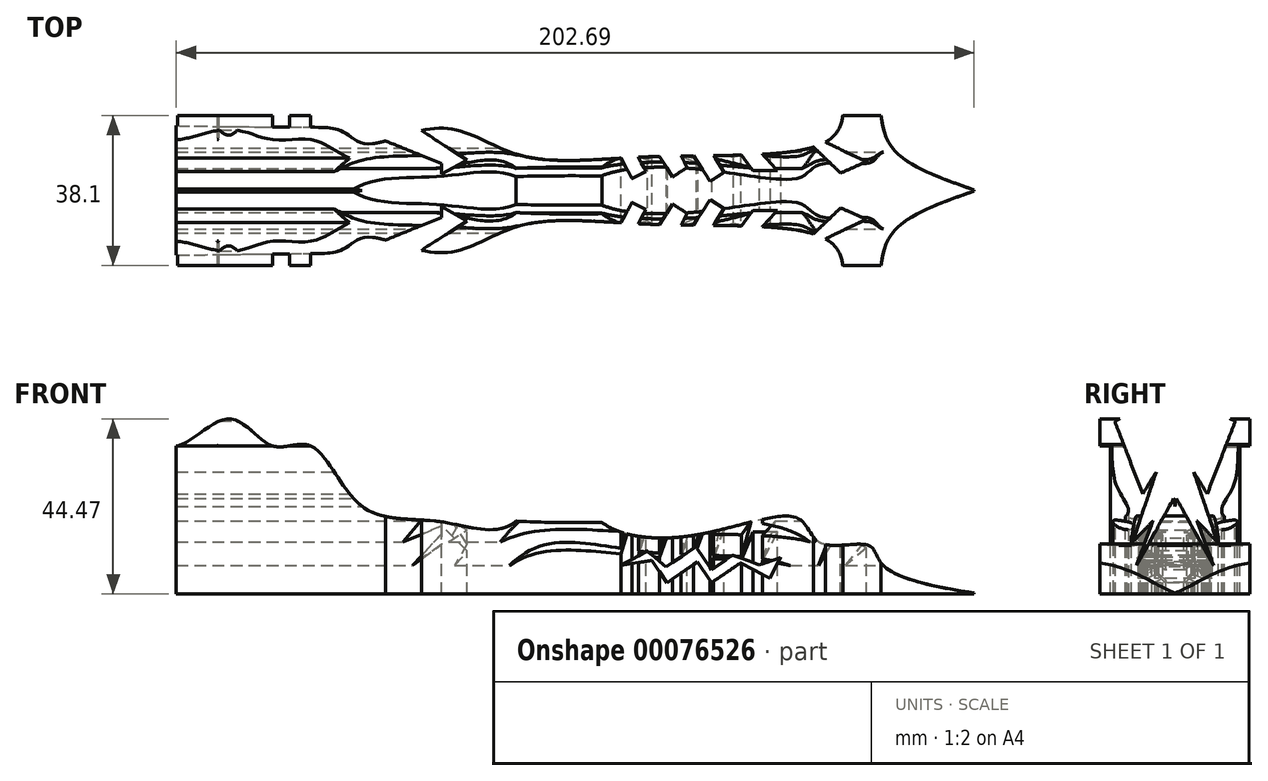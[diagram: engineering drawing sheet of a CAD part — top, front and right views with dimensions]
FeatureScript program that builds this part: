
annotation { "Feature Type Name" : "Feature", "Feature Type Description" : "" }
export const myFeature = defineFeature(function(context is Context, id is Id, definition is map)
    precondition{}
    {
        {
            var Q0;
            Q0=qCreatedBy(makeId("Front.planeOp"),FACE);
            var sketch = newSketch(context, id + "F0", { "sketchPlane" : qUnion([Q0])});
            skLineSegment(sketch, "E0", {"start": v(-67.36, 23) * mm, "end": v(-67.36, -37.65) * mm});
            skLineSegment(sketch, "E1", {"start": v(-67.36, -37.65) * mm, "end": v(135.33, -37.65) * mm});
            skLineSegment(sketch, "E2", {"start": v(135.33, -37.65) * mm, "end": v(135.33, -19.94) * mm});
            skLineSegment(sketch, "E3", {"start": v(135.33, -19.94) * mm, "end": v(-67.36, 23) * mm});
            skSolve(sketch);
        }
        {
            var Q0;
            Q0=makeQuery(id+"F0.imprint","IMPRINT",FACE,{"disambiguationData":[TD([[makeQuery(id+"F0.imprint","IMPRINT",EDGE,{"derivedFrom":sQuery(id+"F0.wireOp",EDGE,"E0")}),1.0]])]});
            extrude(context, id + "F1", {"entities" : qUnion([Q0]), "endBound" : BoundingType.SYMMETRIC, "depth" : 38.1 * mm});
        }
        {
            var Q0;
            Q0=qCreatedBy(makeId("Front.planeOp"),FACE);
            var sketch = newSketch(context, id + "F2", { "sketchPlane" : qUnion([Q0])});
            skFitSpline(sketch, "E4", {"points": [v(-67.52, 10.01) * mm, v(-37.25, 9.08) * mm, v(-13.04, -13.04) * mm, v(96.84, -16.76) * mm, v(119.66, -21.65) * mm, v(136.89, -38.41) * mm, v(148.53, -53.78) * mm, v(0, -97.08) * mm, v(-109.89, -27.47) * mm, v(-68.68, -141.31) * mm, v(197.42, -89.86) * mm, v(91.72, 90.8) * mm, v(-73.1, 52.85) * mm, v(-99.88, 21.65) * mm, v(-67.52, 10.01) * mm]});
            skSolve(sketch);
        }
        {
            var Q0;
            Q0=makeQuery(id+"F2.imprint","IMPRINT",FACE,{"disambiguationData":[TD([[makeQuery(id+"F2.imprint","IMPRINT",EDGE,{"derivedFrom":sQuery(id+"F2.wireOp",EDGE,"E4")}),1.0]])]});
            extrude(context, id + "F3", {"entities" : qUnion([Q0]), "operationType" : NewBodyOperationType.REMOVE, "endBound" : BoundingType.SYMMETRIC, "oppositeDirection" : true, "depth" : 38.1 * mm});
        }
        {
            var Q0;
            Q0=qCreatedBy(makeId("Top.planeOp"),FACE);
            var sketch = newSketch(context, id + "F4", { "sketchPlane" : qUnion([Q0])});
            skFitSpline(sketch, "E5", {"points": [v(-73.1, 16.53) * mm, v(-34.7, 16.06) * mm, v(-24.91, 14.9) * mm, v(-19.1, 11.87) * mm, v(0, 15.83) * mm, v(19.55, 9.08) * mm, v(54, 8.61) * mm, v(95.68, 11.4) * mm, v(101.97, 19.1) * mm, v(102.9, 29.1) * mm, v(109.42, 27.94) * mm, v(111.74, 18.86) * mm, v(115.7, 9.55) * mm, v(135.72, 0) * mm], "startDerivative": vector(378.98, -5.81) * mm, "endDerivative": vector(270.52, -94.72) * mm});
            skFitSpline(sketch, "E6.MirrorCS", {"points": [v(-73.1, -16.53) * mm, v(-34.7, -16.06) * mm, v(-24.91, -14.9) * mm, v(-19.1, -11.87) * mm, v(0, -15.83) * mm, v(19.55, -9.08) * mm, v(54, -8.61) * mm, v(95.68, -11.4) * mm, v(101.97, -19.1) * mm, v(102.9, -29.1) * mm, v(109.42, -27.94) * mm, v(111.74, -18.86) * mm, v(115.7, -9.55) * mm, v(135.72, 0) * mm], "startDerivative": vector(378.98, 5.81) * mm, "endDerivative": vector(270.52, 94.72) * mm});
            skLineSegment(sketch, "E7", {"start": v(-73.1, -16.53) * mm, "end": v(-73.1, -54.3) * mm});
            skLineSegment(sketch, "E8", {"start": v(-73.1, -54.3) * mm, "end": v(204.06, -34.02) * mm});
            skLineSegment(sketch, "E9", {"start": v(204.06, -34.02) * mm, "end": v(136.25, 78.53) * mm});
            skLineSegment(sketch, "E10", {"start": v(136.25, 78.53) * mm, "end": v(-81.16, 49.17) * mm});
            skLineSegment(sketch, "E11", {"start": v(-81.16, 49.17) * mm, "end": v(-73.1, 16.53) * mm});
            skSolve(sketch);
        }
        {
            var Q0;
            Q0=makeQuery(id+"F4.imprint","IMPRINT",FACE,{"disambiguationData":[TD([[makeQuery(id+"F4.imprint","IMPRINT",EDGE,{"derivedFrom":sQuery(id+"F4.wireOp",EDGE,"E5")}),1.0]])]});
            extrude(context, id + "F5", {"entities" : qUnion([Q0]), "operationType" : NewBodyOperationType.REMOVE, "endBound" : BoundingType.THROUGH_ALL, "oppositeDirection" : true, "depth" : 25.4 * mm});
        }
        {
            var Q0;
            Q0=qCreatedBy(makeId("Top.planeOp"),FACE);
            var sketch = newSketch(context, id + "F6", { "sketchPlane" : qUnion([Q0])});
            skLineSegment(sketch, "E12", {"start": v(94.91, 13.54) * mm, "end": v(107.95, 7.32) * mm});
            skLineSegment(sketch, "E13", {"start": v(107.95, 7.32) * mm, "end": v(101.43, 4.42) * mm});
            skPoint(sketch, "E13.endSnap0", {"position": v(101.43, 10.43) * mm});
            skLineSegment(sketch, "E14", {"start": v(101.43, 4.42) * mm, "end": v(86.62, 18.64) * mm});
            skLineSegment(sketch, "E15", {"start": v(86.62, 18.64) * mm, "end": v(94.91, 13.54) * mm});
            skLineSegment(sketch, "E16.MirrorCS", {"start": v(101.43, -4.42) * mm, "end": v(86.62, -18.64) * mm});
            skLineSegment(sketch, "E17.MirrorCS", {"start": v(107.95, -7.32) * mm, "end": v(101.43, -4.42) * mm});
            skLineSegment(sketch, "E18.MirrorCS", {"start": v(94.91, -13.54) * mm, "end": v(107.95, -7.32) * mm});
            skLineSegment(sketch, "E19.MirrorCS", {"start": v(86.62, -18.64) * mm, "end": v(94.91, -13.54) * mm});
            skSolve(sketch);
        }
        {
            var Q0;
            Q0=qCreatedBy(makeId("Top.planeOp"),FACE);
            var sketch = newSketch(context, id + "F7", { "sketchPlane" : qUnion([Q0])});
            skLineSegment(sketch, "E20", {"start": v(78.2, 12.72) * mm, "end": v(85.44, 5.08) * mm});
            skLineSegment(sketch, "E21", {"start": v(85.44, 5.08) * mm, "end": v(79.12, 5.08) * mm});
            skLineSegment(sketch, "E22", {"start": v(79.12, 5.08) * mm, "end": v(70.92, 16.06) * mm});
            skLineSegment(sketch, "E23", {"start": v(70.92, 16.06) * mm, "end": v(78.2, 12.72) * mm});
            skLineSegment(sketch, "E24", {"start": v(65.06, 15.1) * mm, "end": v(71.84, 4.63) * mm});
            skLineSegment(sketch, "E25", {"start": v(71.84, 4.63) * mm, "end": v(68.27, 2.32) * mm});
            skLineSegment(sketch, "E26", {"start": v(68.27, 2.32) * mm, "end": v(60, 15.12) * mm});
            skLineSegment(sketch, "E27", {"start": v(60, 15.12) * mm, "end": v(65.06, 15.1) * mm});
            skLineSegment(sketch, "E28", {"start": v(62.45, 5.83) * mm, "end": v(58.77, 3.46) * mm});
            skLineSegment(sketch, "E29", {"start": v(58.77, 3.46) * mm, "end": v(51.13, 15.27) * mm});
            skLineSegment(sketch, "E30", {"start": v(51.13, 15.27) * mm, "end": v(57.58, 15.27) * mm});
            skLineSegment(sketch, "E31", {"start": v(57.58, 15.27) * mm, "end": v(62.45, 5.83) * mm});
            skLineSegment(sketch, "E32", {"start": v(48.56, 11.18) * mm, "end": v(51.93, 4.88) * mm});
            skLineSegment(sketch, "E33", {"start": v(51.93, 4.88) * mm, "end": v(48.44, 3.02) * mm});
            skLineSegment(sketch, "E34", {"start": v(48.44, 3.02) * mm, "end": v(42.75, 13.7) * mm});
            skLineSegment(sketch, "E35", {"start": v(42.75, 13.7) * mm, "end": v(48.56, 11.18) * mm});
            skLineSegment(sketch, "E36", {"start": v(-18.37, 14.29) * mm, "end": v(0, 6.83) * mm});
            skLineSegment(sketch, "E37", {"start": v(0, 6.83) * mm, "end": v(0, 4.12) * mm});
            skLineSegment(sketch, "E38", {"start": v(0, 4.12) * mm, "end": v(6.58, 7.77) * mm});
            skLineSegment(sketch, "E39", {"start": v(6.58, 7.77) * mm, "end": v(-18.03, 23.44) * mm});
            skLineSegment(sketch, "E40", {"start": v(-18.03, 23.44) * mm, "end": v(-18.37, 14.29) * mm});
            skLineSegment(sketch, "E41.MirrorCS", {"start": v(6.58, -7.77) * mm, "end": v(-18.03, -23.44) * mm});
            skLineSegment(sketch, "E42.MirrorCS", {"start": v(-18.37, -14.29) * mm, "end": v(0, -6.83) * mm});
            skLineSegment(sketch, "E43.MirrorCS", {"start": v(-18.03, -23.44) * mm, "end": v(-18.37, -14.29) * mm});
            skLineSegment(sketch, "E44.MirrorCS", {"start": v(0, -4.12) * mm, "end": v(6.58, -7.77) * mm});
            skLineSegment(sketch, "E45.MirrorCS", {"start": v(0, -6.83) * mm, "end": v(0, -4.12) * mm});
            skLineSegment(sketch, "E46.MirrorCS", {"start": v(48.44, -3.02) * mm, "end": v(42.75, -13.7) * mm});
            skLineSegment(sketch, "E47.MirrorCS", {"start": v(42.75, -13.7) * mm, "end": v(48.56, -11.18) * mm});
            skLineSegment(sketch, "E48.MirrorCS", {"start": v(48.56, -11.18) * mm, "end": v(51.93, -4.88) * mm});
            skLineSegment(sketch, "E49.MirrorCS", {"start": v(51.93, -4.88) * mm, "end": v(48.44, -3.02) * mm});
            skLineSegment(sketch, "E50.MirrorCS", {"start": v(62.45, -5.83) * mm, "end": v(58.77, -3.46) * mm});
            skLineSegment(sketch, "E51.MirrorCS", {"start": v(58.77, -3.46) * mm, "end": v(51.13, -15.27) * mm});
            skLineSegment(sketch, "E52.MirrorCS", {"start": v(57.58, -15.27) * mm, "end": v(62.45, -5.83) * mm});
            skLineSegment(sketch, "E53.MirrorCS", {"start": v(51.13, -15.27) * mm, "end": v(57.58, -15.27) * mm});
            skLineSegment(sketch, "E54.MirrorCS", {"start": v(60, -15.12) * mm, "end": v(65.06, -15.1) * mm});
            skLineSegment(sketch, "E55.MirrorCS", {"start": v(68.27, -2.32) * mm, "end": v(60, -15.12) * mm});
            skLineSegment(sketch, "E56.MirrorCS", {"start": v(71.84, -4.63) * mm, "end": v(68.27, -2.32) * mm});
            skLineSegment(sketch, "E57.MirrorCS", {"start": v(65.06, -15.1) * mm, "end": v(71.84, -4.63) * mm});
            skLineSegment(sketch, "E58.MirrorCS", {"start": v(79.12, -5.08) * mm, "end": v(70.92, -16.06) * mm});
            skLineSegment(sketch, "E59.MirrorCS", {"start": v(70.92, -16.06) * mm, "end": v(78.2, -12.72) * mm});
            skLineSegment(sketch, "E60.MirrorCS", {"start": v(78.2, -12.72) * mm, "end": v(85.44, -5.08) * mm});
            skLineSegment(sketch, "E61.MirrorCS", {"start": v(85.44, -5.08) * mm, "end": v(79.12, -5.08) * mm});
            skSolve(sketch);
        }
        {
            var Q0;
            Q0=makeQuery(id+"F6.imprint","IMPRINT",FACE,{"disambiguationData":[TD([[makeQuery(id+"F6.imprint","IMPRINT",EDGE,{"derivedFrom":sQuery(id+"F6.wireOp",EDGE,"E12")}),-1.0]])]});
            var Q1;
            Q1=makeQuery(id+"F7.imprint","IMPRINT",FACE,{"disambiguationData":[TD([[makeQuery(id+"F7.imprint","IMPRINT",EDGE,{"derivedFrom":sQuery(id+"F7.wireOp",EDGE,"E58.MirrorCS")}),1.0]])]});
            var Q2;
            Q2=makeQuery(id+"F7.imprint","IMPRINT",FACE,{"disambiguationData":[TD([[makeQuery(id+"F7.imprint","IMPRINT",EDGE,{"derivedFrom":sQuery(id+"F7.wireOp",EDGE,"E41.MirrorCS")}),-1.0]])]});
            var Q3;
            Q3=makeQuery(id+"F7.imprint","IMPRINT",FACE,{"disambiguationData":[TD([[makeQuery(id+"F7.imprint","IMPRINT",EDGE,{"derivedFrom":sQuery(id+"F7.wireOp",EDGE,"E20")}),-1.0]])]});
            var Q4;
            Q4=makeQuery(id+"F7.imprint","IMPRINT",FACE,{"disambiguationData":[TD([[makeQuery(id+"F7.imprint","IMPRINT",EDGE,{"derivedFrom":sQuery(id+"F7.wireOp",EDGE,"E32")}),-1.0]])]});
            var Q5;
            Q5=makeQuery(id+"F7.imprint","IMPRINT",FACE,{"disambiguationData":[TD([[makeQuery(id+"F7.imprint","IMPRINT",EDGE,{"derivedFrom":sQuery(id+"F7.wireOp",EDGE,"E46.MirrorCS")}),1.0]])]});
            var Q6;
            Q6=makeQuery(id+"F7.imprint","IMPRINT",FACE,{"disambiguationData":[TD([[makeQuery(id+"F7.imprint","IMPRINT",EDGE,{"derivedFrom":sQuery(id+"F7.wireOp",EDGE,"E36")}),1.0]])]});
            var Q7;
            Q7=makeQuery(id+"F7.imprint","IMPRINT",FACE,{"disambiguationData":[TD([[makeQuery(id+"F7.imprint","IMPRINT",EDGE,{"derivedFrom":sQuery(id+"F7.wireOp",EDGE,"E50.MirrorCS")}),1.0]])]});
            var Q8;
            Q8=makeQuery(id+"F7.imprint","IMPRINT",FACE,{"disambiguationData":[TD([[makeQuery(id+"F7.imprint","IMPRINT",EDGE,{"derivedFrom":sQuery(id+"F7.wireOp",EDGE,"E28")}),-1.0]])]});
            var Q9;
            Q9=makeQuery(id+"F7.imprint","IMPRINT",FACE,{"disambiguationData":[TD([[makeQuery(id+"F7.imprint","IMPRINT",EDGE,{"derivedFrom":sQuery(id+"F7.wireOp",EDGE,"E24")}),-1.0]])]});
            var Q10;
            Q10=makeQuery(id+"F7.imprint","IMPRINT",FACE,{"disambiguationData":[TD([[makeQuery(id+"F7.imprint","IMPRINT",EDGE,{"derivedFrom":sQuery(id+"F7.wireOp",EDGE,"E54.MirrorCS")}),1.0]])]});
            var Q11;
            Q11=makeQuery(id+"F6.imprint","IMPRINT",FACE,{"disambiguationData":[TD([[makeQuery(id+"F6.imprint","IMPRINT",EDGE,{"derivedFrom":sQuery(id+"F6.wireOp",EDGE,"E16.MirrorCS")}),1.0]])]});
            extrude(context, id + "F8", {"entities" : qUnion([Q0, Q1, Q2, Q3, Q4, Q5, Q6, Q7, Q8, Q9, Q10, Q11]), "operationType" : NewBodyOperationType.REMOVE, "endBound" : BoundingType.SYMMETRIC, "oppositeDirection" : true, "depth" : 355.6 * mm});
        }
        {
            var Q0;
            Q0=qCreatedBy(makeId("Right.planeOp"),FACE);
            var sketch = newSketch(context, id + "F9", { "sketchPlane" : qUnion([Q0])});
            skFitSpline(sketch, "E62", {"points": [v(-25.14, 15.13) * mm, v(-9.78, 13.04) * mm, v(0, -15.37) * mm], "startDerivative": vector(40.92, 4.14) * mm, "endDerivative": vector(11, -61.55) * mm});
            skFitSpline(sketch, "E63.MirrorCS", {"points": [v(25.14, 15.13) * mm, v(9.78, 13.04) * mm, v(0, -15.37) * mm], "startDerivative": vector(-40.92, 4.14) * mm, "endDerivative": vector(-11, -61.55) * mm});
            skFitSpline(sketch, "E64.MirrorCS", {"points": [v(25.14, 15.13) * mm, v(9.78, 13.04) * mm, v(0, -15.37) * mm], "startDerivative": vector(-40.92, 4.14) * mm, "endDerivative": vector(-11, -61.55) * mm});
            skLineSegment(sketch, "E65", {"start": v(25.14, 15.13) * mm, "end": v(0, 34.12) * mm});
            skLineSegment(sketch, "E66", {"start": v(0, 34.12) * mm, "end": v(-25.14, 15.13) * mm});
            skSolve(sketch);
        }
        {
            var Q0;
            Q0=makeQuery(id+"F9.imprint","IMPRINT",FACE,{"disambiguationData":[TD([[makeQuery(id+"F9.imprint","IMPRINT",EDGE,{"derivedFrom":sQuery(id+"F9.wireOp",EDGE,"E62")}),1.0]])]});
            extrude(context, id + "F10", {"entities" : qUnion([Q0]), "operationType" : NewBodyOperationType.REMOVE, "endBound" : BoundingType.SYMMETRIC, "oppositeDirection" : true, "depth" : 355.6 * mm});
        }
        {
            var Q0;
            Q0=qCreatedBy(makeId("Right.planeOp"),FACE);
            var sketch = newSketch(context, id + "F11", { "sketchPlane" : qUnion([Q0])});
            skLineSegment(sketch, "E67", {"start": v(0, 0) * mm, "end": v(7.6, 0) * mm});
            skLineSegment(sketch, "E68", {"start": v(7.6, 0) * mm, "end": v(10.72, 8.1) * mm});
            skLineSegment(sketch, "E69", {"start": v(10.72, 8.1) * mm, "end": v(15.33, 6.32) * mm});
            skLineSegment(sketch, "E70", {"start": v(15.33, 6.32) * mm, "end": v(8.2, -12.23) * mm});
            skLineSegment(sketch, "E71", {"start": v(8.2, -12.23) * mm, "end": v(4.76, -6.61) * mm});
            skLineSegment(sketch, "E72", {"start": v(4.76, -6.61) * mm, "end": v(10.76, -24.44) * mm});
            skLineSegment(sketch, "E73", {"start": v(10.76, -24.44) * mm, "end": v(5.62, -19.13) * mm});
            skLineSegment(sketch, "E74", {"start": v(5.62, -19.13) * mm, "end": v(9.82, -30.44) * mm});
            skLineSegment(sketch, "E75", {"start": v(9.82, -30.44) * mm, "end": v(0, -12.78) * mm});
            skLineSegment(sketch, "E76.MirrorCS", {"start": v(-7.6, 0) * mm, "end": v(-10.72, 8.1) * mm});
            skLineSegment(sketch, "E77.MirrorCS", {"start": v(0, 0) * mm, "end": v(-7.6, 0) * mm});
            skLineSegment(sketch, "E78.MirrorCS", {"start": v(-15.33, 6.32) * mm, "end": v(-8.2, -12.23) * mm});
            skLineSegment(sketch, "E79.MirrorCS", {"start": v(-10.72, 8.1) * mm, "end": v(-15.33, 6.32) * mm});
            skLineSegment(sketch, "E80.MirrorCS", {"start": v(-8.2, -12.23) * mm, "end": v(-4.76, -6.61) * mm});
            skLineSegment(sketch, "E81.MirrorCS", {"start": v(-4.76, -6.61) * mm, "end": v(-10.76, -24.44) * mm});
            skLineSegment(sketch, "E82.MirrorCS", {"start": v(-10.76, -24.44) * mm, "end": v(-5.62, -19.13) * mm});
            skLineSegment(sketch, "E83.MirrorCS", {"start": v(-5.62, -19.13) * mm, "end": v(-9.82, -30.44) * mm});
            skLineSegment(sketch, "E84.MirrorCS", {"start": v(-9.82, -30.44) * mm, "end": v(0, -12.78) * mm});
            skSolve(sketch);
        }
        {
            var Q0;
            Q0=makeQuery(id+"F11.imprint","IMPRINT",FACE,{"disambiguationData":[TD([[makeQuery(id+"F11.imprint","IMPRINT",EDGE,{"derivedFrom":sQuery(id+"F11.wireOp",EDGE,"E67")}),-1.0]])]});
            extrude(context, id + "F12", {"entities" : qUnion([Q0]), "operationType" : NewBodyOperationType.REMOVE, "endBound" : BoundingType.SYMMETRIC, "oppositeDirection" : true, "depth" : 12700 * mm});
        }
        {
            var Q0;
            {var subQ0=sQuery(id+"F0.wireOp",EDGE,"E0");Q0=makeQuery(id+"F5.boolean.opBoolean","SPLIT",FACE,{"disambiguationData":[TD([makeQuery(id+"F1.opExtrude","SWEPT_FACE",FACE,{"disambiguationData":[OSD([subQ0])]})])],"derivedFrom":makeQuery(id+"F1.opExtrude","CAP_FACE",FACE,{"disambiguationData":[OSD([subQ0,sQuery(id+"F0.wireOp",EDGE,"E1"),sQuery(id+"F0.wireOp",EDGE,"E2"),sQuery(id+"F0.wireOp",EDGE,"E3")])],"isStart":false})});}
            var sketch = newSketch(context, id + "F13", { "sketchPlane" : qUnion([Q0])});
            skPoint(sketch, "E85.4.internal.snap0", {"position": v(-47.88, 0) * mm});
            skPoint(sketch, "E85.6.internal.snap0", {"position": v(-47.88, 0) * mm});
            skFitSpline(sketch, "E85", {"points": [v(-56.66, 0) * mm, v(-60.41, -6.56) * mm, v(-61.2, -19.55) * mm, v(-53.68, -12.2) * mm, v(-47.88, -15.63) * mm, v(-62.92, -24.71) * mm, v(-47.88, -29.72) * mm, v(-36.94, -19.4) * mm, v(-30.68, -31.29) * mm, v(-8.76, -27.69) * mm, v(34.28, -34.26) * mm, v(37.72, -26.43) * mm, v(17.85, -23.46) * mm, v(-19.1, -23.77) * mm, v(-26.76, -11.72) * mm, v(-41.63, -15.32) * mm, v(-31.46, -7.03) * mm, v(-56.03, -7.65) * mm, v(-56.66, 0) * mm]});
            skSolve(sketch);
        }
        {
            var Q0;
            {var subQ0=sQuery(id+"F13.wireOp",EDGE,"E85");var subQ1=makeQuery(id+"F5.boolean.opBoolean","INTERSECT",EDGE,{"derivedFrom":[makeQuery(id+"F1.opExtrude","CAP_FACE",FACE,{"disambiguationData":[OSD([sQuery(id+"F0.wireOp",EDGE,"E0"),sQuery(id+"F0.wireOp",EDGE,"E1"),sQuery(id+"F0.wireOp",EDGE,"E2"),sQuery(id+"F0.wireOp",EDGE,"E3")])],"isStart":false}),makeQuery(id+"F5.opExtrude","CAP_FACE",FACE,{"disambiguationData":[OSD([sQuery(id+"F4.wireOp",EDGE,"E5"),sQuery(id+"F4.wireOp",EDGE,"E6.MirrorCS"),sQuery(id+"F4.wireOp",EDGE,"E7"),sQuery(id+"F4.wireOp",EDGE,"E8"),sQuery(id+"F4.wireOp",EDGE,"E9"),sQuery(id+"F4.wireOp",EDGE,"E10"),sQuery(id+"F4.wireOp",EDGE,"E11")])],"isStart":true})]});var subQ2=makeQuery(id+"F13.imprint","INTERSECT",VERTEX,{"disambiguationData":[OD(0.0)],"derivedFrom":[subQ1,subQ0]});Q0=makeQuery(id+"F13.imprint","IMPRINT",FACE,{"disambiguationData":[TD([[makeQuery(id+"F13.imprint","IMPRINT",EDGE,{"disambiguationData":[TD([[subQ2,-1.0]])],"derivedFrom":subQ0}),1.0]])]});}
            extrude(context, id + "F14", {"entities" : qUnion([Q0]), "operationType" : NewBodyOperationType.REMOVE, "endBound" : BoundingType.THROUGH_ALL, "oppositeDirection" : true, "depth" : 25.4 * mm});
        }
        {
            var Q0;
            {var subQ0=sQuery(id+"F0.wireOp",EDGE,"E0");Q0=makeQuery(id+"F5.boolean.opBoolean","SPLIT",FACE,{"disambiguationData":[TD([makeQuery(id+"F1.opExtrude","SWEPT_FACE",FACE,{"disambiguationData":[OSD([subQ0])]})])],"derivedFrom":makeQuery(id+"F1.opExtrude","CAP_FACE",FACE,{"disambiguationData":[OSD([subQ0,sQuery(id+"F0.wireOp",EDGE,"E1"),sQuery(id+"F0.wireOp",EDGE,"E2"),sQuery(id+"F0.wireOp",EDGE,"E3")])],"isStart":false})});}
            var sketch = newSketch(context, id + "F15", { "sketchPlane" : qUnion([Q0])});
            skFitSpline(sketch, "E86", {"points": [v(45.03, 0) * mm, v(38.64, -17.24) * mm, v(63.42, -22.85) * mm, v(90.69, -18.49) * mm, v(96.45, -24.72) * mm, v(108.6, -25.34) * mm, v(112.5, -30.64) * mm, v(140.55, -38.12) * mm, v(156.13, -41.86) * mm, v(172.18, -46.38) * mm, v(160.5, -12.88) * mm, v(45.03, 0) * mm]});
            skSolve(sketch);
        }
        {
            var Q0;
            Q0=makeQuery(id+"F15.imprint","IMPRINT",FACE,{"disambiguationData":[TD([[makeQuery(id+"F15.imprint","IMPRINT",EDGE,{"derivedFrom":sQuery(id+"F15.wireOp",EDGE,"E86")}),1.0]])]});
            extrude(context, id + "F16", {"entities" : qUnion([Q0]), "operationType" : NewBodyOperationType.REMOVE, "endBound" : BoundingType.THROUGH_ALL, "oppositeDirection" : true, "depth" : 27940 * mm});
        }
        {
            var Q0;
            {var subQ0=sQuery(id+"F0.wireOp",EDGE,"E0");Q0=makeQuery(id+"F5.boolean.opBoolean","SPLIT",FACE,{"disambiguationData":[TD([makeQuery(id+"F1.opExtrude","SWEPT_FACE",FACE,{"disambiguationData":[OSD([subQ0])]})])],"derivedFrom":makeQuery(id+"F1.opExtrude","CAP_FACE",FACE,{"disambiguationData":[OSD([subQ0,sQuery(id+"F0.wireOp",EDGE,"E1"),sQuery(id+"F0.wireOp",EDGE,"E2"),sQuery(id+"F0.wireOp",EDGE,"E3")])],"isStart":false})});}
            var sketch = newSketch(context, id + "F17", { "sketchPlane" : qUnion([Q0])});
            skLineSegment(sketch, "E87", {"start": v(45.49, -30.41) * mm, "end": v(52.28, -26.73) * mm});
            skLineSegment(sketch, "E88", {"start": v(52.28, -26.73) * mm, "end": v(57.13, -30.8) * mm});
            skLineSegment(sketch, "E89", {"start": v(57.13, -30.8) * mm, "end": v(64.63, -25.63) * mm});
            skLineSegment(sketch, "E90", {"start": v(64.63, -25.63) * mm, "end": v(68.67, -31.5) * mm});
            skLineSegment(sketch, "E91", {"start": v(68.67, -31.5) * mm, "end": v(74.04, -27.8) * mm});
            skLineSegment(sketch, "E92", {"start": v(74.04, -27.8) * mm, "end": v(80.73, -30.28) * mm});
            skLineSegment(sketch, "E93", {"start": v(80.73, -30.28) * mm, "end": v(86.16, -28.4) * mm});
            skLineSegment(sketch, "E94", {"start": v(86.16, -28.4) * mm, "end": v(83.45, -33.65) * mm});
            skPoint(sketch, "E94.endSnap0", {"position": v(83.45, -29.35) * mm});
            skLineSegment(sketch, "E95", {"start": v(83.45, -33.65) * mm, "end": v(75.97, -29.77) * mm});
            skLineSegment(sketch, "E96", {"start": v(75.97, -29.77) * mm, "end": v(68.67, -34.75) * mm});
            skLineSegment(sketch, "E97", {"start": v(68.67, -34.75) * mm, "end": v(65.04, -29.47) * mm});
            skLineSegment(sketch, "E98", {"start": v(65.04, -29.47) * mm, "end": v(57.34, -34.78) * mm});
            skLineSegment(sketch, "E99", {"start": v(57.34, -34.78) * mm, "end": v(53.45, -29.13) * mm});
            skLineSegment(sketch, "E100", {"start": v(53.45, -29.13) * mm, "end": v(45.49, -30.41) * mm});
            skSolve(sketch);
        }
        {
            var Q0;
            Q0=makeQuery(id+"F17.imprint","IMPRINT",FACE,{"disambiguationData":[TD([[makeQuery(id+"F17.imprint","IMPRINT",EDGE,{"derivedFrom":sQuery(id+"F17.wireOp",EDGE,"E87")}),-1.0]])]});
            extrude(context, id + "F18", {"entities" : qUnion([Q0]), "operationType" : NewBodyOperationType.REMOVE, "endBound" : BoundingType.SYMMETRIC, "oppositeDirection" : true, "depth" : 27940 * mm});
        }
        {
            var Q0;
            Q0=qCreatedBy(makeId("Front.planeOp"),FACE);
            var sketch = newSketch(context, id + "F19", { "sketchPlane" : qUnion([Q0])});
            skFitSpline(sketch, "E101", {"points": [v(-68.74, 0) * mm, v(-54.37, 6.8) * mm, v(-42.9, 0) * mm, v(-33.22, 0) * mm, v(-20.22, -15.31) * mm, v(0, -19.32) * mm, v(20, -18.21) * mm, v(13.1, 57.95) * mm, v(-59.76, 53.25) * mm, v(-68.74, 0) * mm]});
            skSolve(sketch);
        }
        {
            var Q0;
            Q0=makeQuery(id+"F19.imprint","IMPRINT",FACE,{"disambiguationData":[TD([[makeQuery(id+"F19.imprint","IMPRINT",EDGE,{"derivedFrom":sQuery(id+"F19.wireOp",EDGE,"E101")}),1.0]])]});
            extrude(context, id + "F20", {"entities" : qUnion([Q0]), "operationType" : NewBodyOperationType.REMOVE, "endBound" : BoundingType.SYMMETRIC, "depth" : 355.6 * mm, "hasSecondDirection" : true, "secondDirectionBound" : SecondDirectionBoundingType.THROUGH_ALL, "secondDirectionOppositeDirection" : true, "secondDirectionDepth" : 25.4 * mm});
        }
        {
            var Q0;
            Q0=qCreatedBy(makeId("Right.planeOp"),FACE);
            var sketch = newSketch(context, id + "F21", { "sketchPlane" : qUnion([Q0])});
            skLineSegment(sketch, "E102", {"start": v(-13.63, 9.03) * mm, "end": v(-10.32, 0) * mm});
            skLineSegment(sketch, "E103", {"start": v(-10.32, 0) * mm, "end": v(0, -3.43) * mm});
            skLineSegment(sketch, "E104", {"start": v(0, -3.43) * mm, "end": v(10.5, 0) * mm});
            skLineSegment(sketch, "E105", {"start": v(10.5, 0) * mm, "end": v(12.3, 15.13) * mm});
            skLineSegment(sketch, "E106", {"start": v(12.3, 15.13) * mm, "end": v(-11.97, 9.03) * mm});
            skPoint(sketch, "E106.endSnap0", {"position": v(-11.97, 4.52) * mm});
            skLineSegment(sketch, "E107", {"start": v(-11.97, 9.03) * mm, "end": v(-13.63, 9.03) * mm});
            skSolve(sketch);
        }
        {
            var Q0;
            Q0=makeQuery(id+"F21.imprint","IMPRINT",FACE,{"disambiguationData":[TD([[makeQuery(id+"F21.imprint","IMPRINT",EDGE,{"derivedFrom":sQuery(id+"F21.wireOp",EDGE,"E102")}),1.0]])]});
            extrude(context, id + "F22", {"entities" : qUnion([Q0]), "operationType" : NewBodyOperationType.REMOVE, "endBound" : BoundingType.SYMMETRIC, "oppositeDirection" : true, "depth" : 115392.2 * mm});
        }
    });
